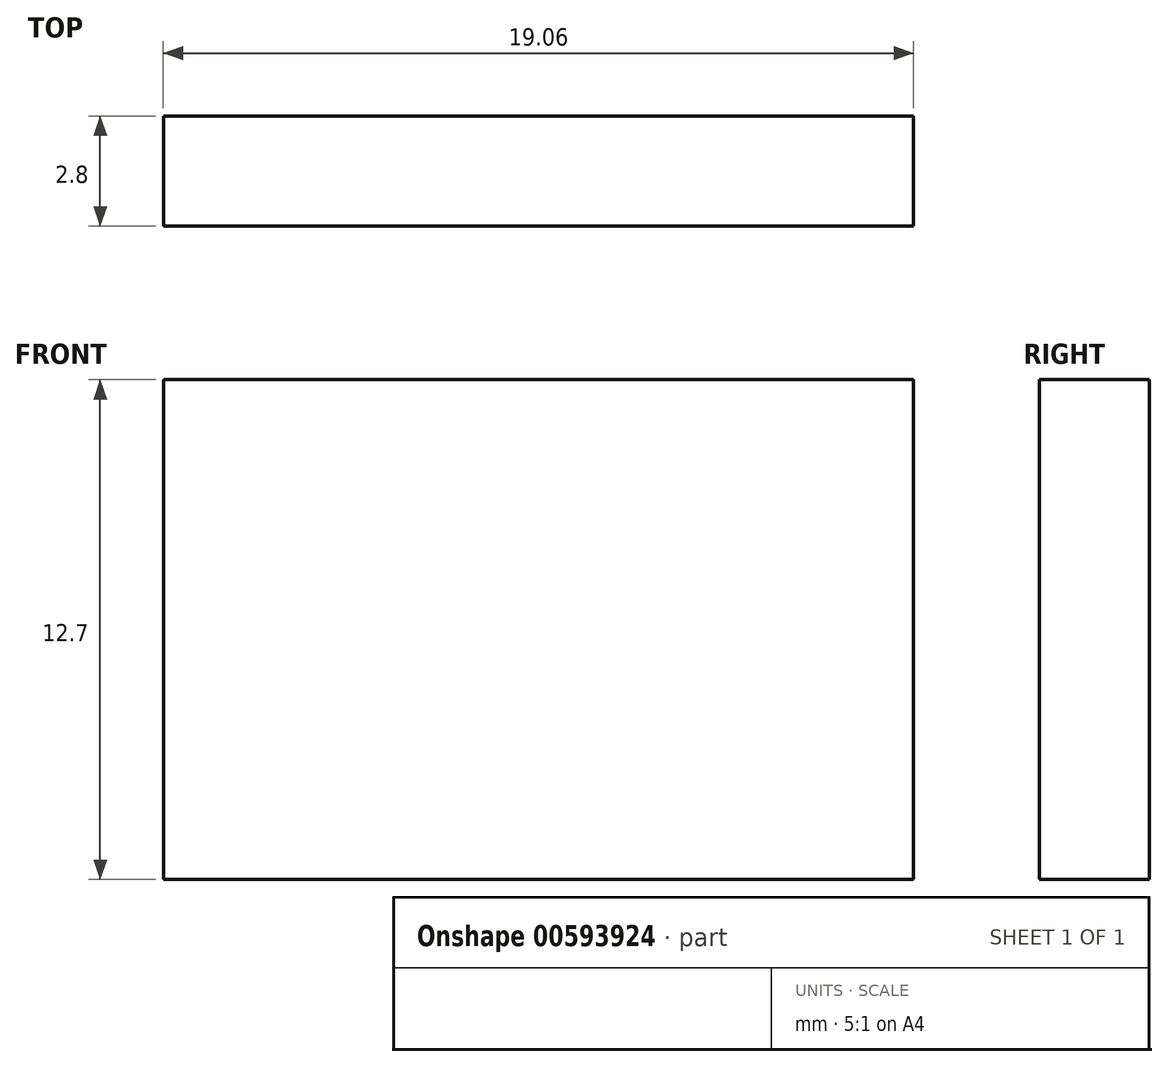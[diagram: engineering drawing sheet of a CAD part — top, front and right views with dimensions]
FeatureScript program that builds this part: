
annotation { "Feature Type Name" : "Feature", "Feature Type Description" : "" }
export const myFeature = defineFeature(function(context is Context, id is Id, definition is map)
    precondition{}
    {
        {
            var Q0;
            Q0=qCreatedBy(makeId("Top.planeOp"),FACE);
            var sketch = newSketch(context, id + "F0", { "sketchPlane" : qUnion([Q0])});
            skLineSegment(sketch, "E0.bottom", {"start": v(9.53, -1.4) * mm, "end": v(-9.53, -1.4) * mm});
            skLineSegment(sketch, "E0.top", {"start": v(9.53, 1.4) * mm, "end": v(-9.53, 1.4) * mm});
            skLineSegment(sketch, "E0.left", {"start": v(9.53, -1.4) * mm, "end": v(9.53, 1.4) * mm});
            skLineSegment(sketch, "E0.right", {"start": v(-9.53, -1.4) * mm, "end": v(-9.53, 1.4) * mm});
            skPoint(sketch, "E0.middle", {"position": v(0, 0) * mm});
            skSolve(sketch);
        }
        {
            var Q0;
            Q0=qSketchRegion(id+"F0",true);
            extrude(context, id + "F1", {"entities" : qUnion([Q0]), "depth" : 12.7 * mm, "offsetDistance" : 25.4 * mm});
        }
    });
